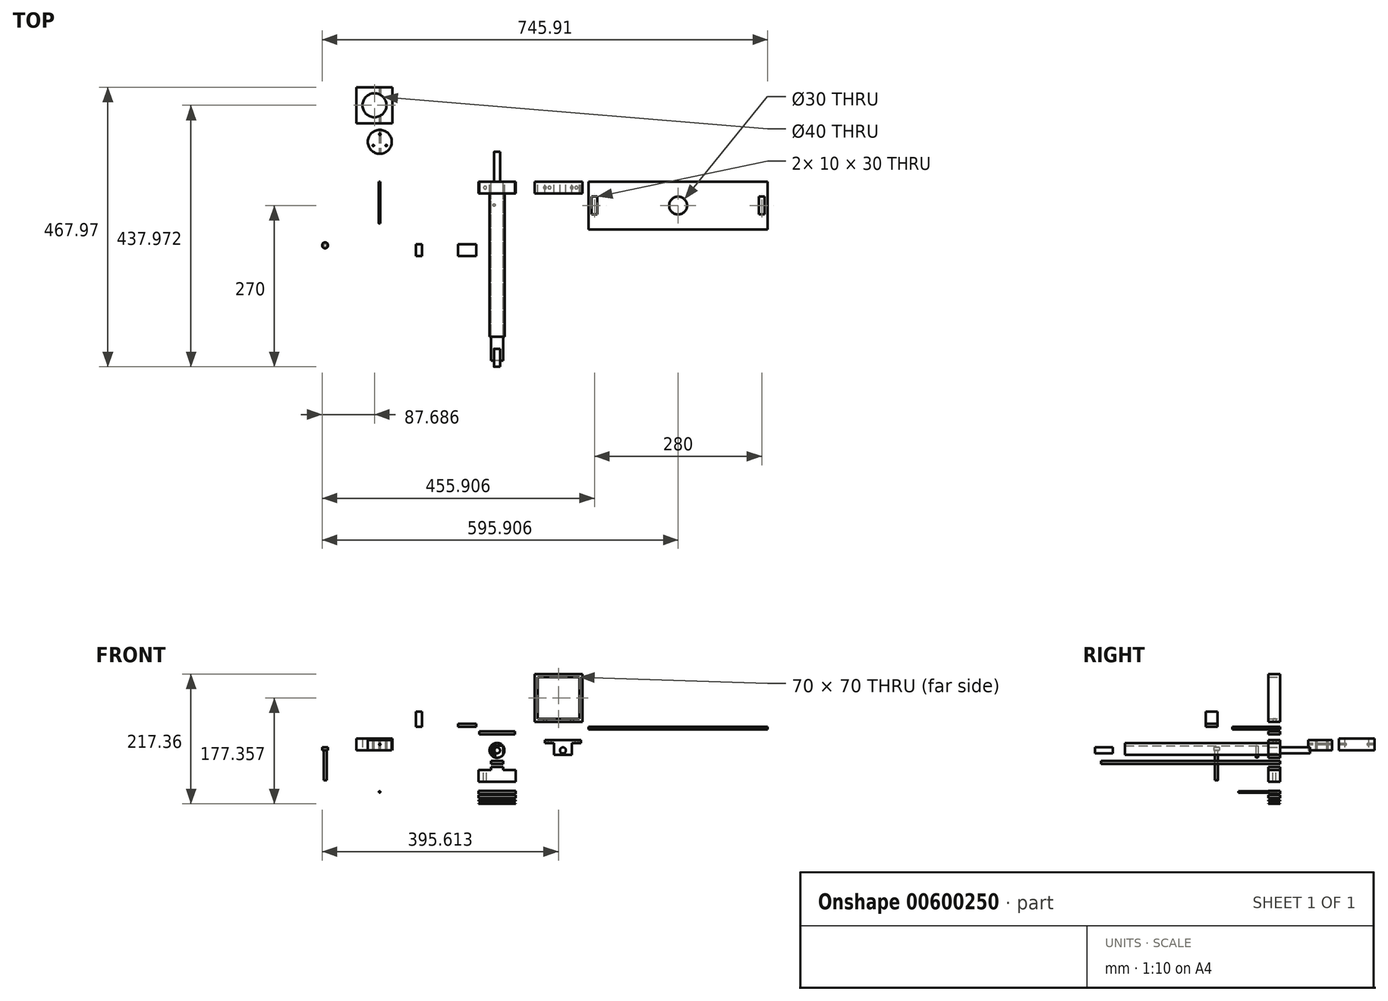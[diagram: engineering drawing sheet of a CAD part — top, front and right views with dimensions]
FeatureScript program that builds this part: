
annotation { "Feature Type Name" : "Feature", "Feature Type Description" : "" }
export const myFeature = defineFeature(function(context is Context, id is Id, definition is map)
    precondition{}
    {
        {
            var Q0;
            Q0=qCreatedBy(makeId("Front.planeOp"),FACE);
            var sketch = newSketch(context, id + "F0", { "sketchPlane" : qUnion([Q0])});
            skCircle(sketch, "E0", {"center": v(0, 0) * mm, "radius": 12.5 * mm});
            skCircle(sketch, "E1", {"center": v(110.3, 0) * mm, "radius": 5 * mm});
            skLineSegment(sketch, "E2.bottom", {"start": v(-30, 31.74) * mm, "end": v(30, 31.74) * mm});
            skLineSegment(sketch, "E2.top", {"start": v(-30, 26.74) * mm, "end": v(30, 26.74) * mm});
            skLineSegment(sketch, "E2.left", {"start": v(-30, 31.74) * mm, "end": v(-30, 26.74) * mm});
            skLineSegment(sketch, "E2.right", {"start": v(30, 31.74) * mm, "end": v(30, 26.74) * mm});
            skPoint(sketch, "E2.middle", {"position": v(0, 29.24) * mm});
            skLineSegment(sketch, "E3", {"start": v(110.3, 10) * mm, "end": v(110.3, -10) * mm, "construction": true});
            skCircle(sketch, "E4", {"center": v(110.3, 0) * mm, "radius": 12.5 * mm, "construction": true});
            skLineSegment(sketch, "E5", {"start": v(97.8, 0) * mm, "end": v(122.8, 0) * mm, "construction": true});
            skLineSegment(sketch, "E6", {"start": v(110.3, 12.5) * mm, "end": v(79.29, 12.5) * mm, "construction": true});
            skLineSegment(sketch, "E7", {"start": v(110.3, 5) * mm, "end": v(79.29, 5) * mm, "construction": true});
            skLineSegment(sketch, "E8", {"start": v(110.3, -5) * mm, "end": v(79.29, -5) * mm, "construction": true});
            skLineSegment(sketch, "E9", {"start": v(110.3, -12.5) * mm, "end": v(79.29, -12.5) * mm, "construction": true});
            skLineSegment(sketch, "E10", {"start": v(110.3, -7.5) * mm, "end": v(125.3, -7.5) * mm});
            skLineSegment(sketch, "E11", {"start": v(110.3, 17.5) * mm, "end": v(140.3, 17.5) * mm});
            skLineSegment(sketch, "E12", {"start": v(125.3, 12.5) * mm, "end": v(140.3, 12.5) * mm});
            skLineSegment(sketch, "E13", {"start": v(125.3, -7.5) * mm, "end": v(125.3, 12.5) * mm});
            skLineSegment(sketch, "E14", {"start": v(140.3, 17.5) * mm, "end": v(140.3, 12.5) * mm});
            skPoint(sketch, "E15.orphan", {"position": v(110.3, 12.5) * mm});
            skLineSegment(sketch, "E16.MirrorCS", {"start": v(95.3, 12.5) * mm, "end": v(80.3, 12.5) * mm});
            skLineSegment(sketch, "E17.MirrorCS", {"start": v(80.3, 17.5) * mm, "end": v(80.3, 12.5) * mm});
            skLineSegment(sketch, "E18.MirrorCS", {"start": v(110.3, 17.5) * mm, "end": v(80.3, 17.5) * mm});
            skLineSegment(sketch, "E19.MirrorCS", {"start": v(95.3, -7.5) * mm, "end": v(95.3, 12.5) * mm});
            skLineSegment(sketch, "E20.MirrorCS", {"start": v(110.3, -7.5) * mm, "end": v(95.3, -7.5) * mm});
            skLineSegment(sketch, "E21.top", {"start": v(0, -27.58) * mm, "end": v(10, -27.58) * mm});
            skLineSegment(sketch, "E22", {"start": v(10.93, -32.58) * mm, "end": v(30.93, -32.58) * mm});
            skLineSegment(sketch, "E23", {"start": v(30.93, -32.58) * mm, "end": v(30.93, -52.58) * mm});
            skLineSegment(sketch, "E24", {"start": v(30.93, -52.58) * mm, "end": v(0, -52.58) * mm});
            skLineSegment(sketch, "E25.MirrorCS", {"start": v(0, -27.58) * mm, "end": v(-10, -27.58) * mm});
            skLineSegment(sketch, "E26.MirrorCS", {"start": v(-10.93, -32.58) * mm, "end": v(-30.93, -32.58) * mm});
            skLineSegment(sketch, "E27.MirrorCS", {"start": v(-30.93, -32.58) * mm, "end": v(-30.93, -52.58) * mm});
            skLineSegment(sketch, "E28.MirrorCS", {"start": v(-30.93, -52.58) * mm, "end": v(0, -52.58) * mm});
            skLineSegment(sketch, "E29", {"start": v(0, -22.52) * mm, "end": v(10, -22.52) * mm});
            skLineSegment(sketch, "E30", {"start": v(10, -22.52) * mm, "end": v(10, -17.52) * mm});
            skLineSegment(sketch, "E31", {"start": v(10, -17.52) * mm, "end": v(0, -17.52) * mm});
            skLineSegment(sketch, "E32.MirrorCS", {"start": v(-10, -17.52) * mm, "end": v(0, -17.52) * mm});
            skLineSegment(sketch, "E33.MirrorCS", {"start": v(0, -22.52) * mm, "end": v(-10, -22.52) * mm});
            skLineSegment(sketch, "E34.MirrorCS", {"start": v(-10, -22.52) * mm, "end": v(-10, -17.52) * mm});
            skLineSegment(sketch, "E35.bottom", {"start": v(137.73, 52.7) * mm, "end": v(67.73, 52.7) * mm});
            skLineSegment(sketch, "E35.top", {"start": v(137.73, 122.7) * mm, "end": v(67.73, 122.7) * mm});
            skLineSegment(sketch, "E35.left", {"start": v(137.73, 52.7) * mm, "end": v(137.73, 122.7) * mm});
            skLineSegment(sketch, "E35.right", {"start": v(67.73, 52.7) * mm, "end": v(67.73, 122.7) * mm});
            skPoint(sketch, "E35.middle", {"position": v(102.73, 87.7) * mm});
            skLineSegment(sketch, "E36.bottom", {"start": v(62.73, 127.7) * mm, "end": v(142.73, 127.7) * mm});
            skLineSegment(sketch, "E36.top", {"start": v(62.73, 47.7) * mm, "end": v(142.73, 47.7) * mm});
            skLineSegment(sketch, "E36.left", {"start": v(62.73, 127.7) * mm, "end": v(62.73, 47.7) * mm});
            skLineSegment(sketch, "E36.right", {"start": v(142.73, 127.7) * mm, "end": v(142.73, 47.7) * mm});
            skLineSegment(sketch, "E37.bottom", {"start": v(-30.93, -79.86) * mm, "end": v(30.93, -79.86) * mm});
            skLineSegment(sketch, "E37.top", {"start": v(-30.93, -74.86) * mm, "end": v(30.93, -74.86) * mm});
            skLineSegment(sketch, "E37.left", {"start": v(-30.93, -79.86) * mm, "end": v(-30.93, -74.86) * mm});
            skLineSegment(sketch, "E37.right", {"start": v(30.93, -79.86) * mm, "end": v(30.93, -74.86) * mm});
            skLineSegment(sketch, "E38.MirrorCS", {"start": v(-30.74, -88.65) * mm, "end": v(31.12, -88.65) * mm});
            skLineSegment(sketch, "E39.MirrorCS", {"start": v(-30.74, -89.65) * mm, "end": v(31.12, -89.65) * mm});
            skLineSegment(sketch, "E40", {"start": v(-30.93, -82.76) * mm, "end": v(30.93, -82.76) * mm});
            skLineSegment(sketch, "E41", {"start": v(30.93, -82.76) * mm, "end": v(30.93, -84.76) * mm});
            skLineSegment(sketch, "E42", {"start": v(30.93, -84.76) * mm, "end": v(-30.93, -84.76) * mm});
            skLineSegment(sketch, "E43", {"start": v(-30.93, -84.76) * mm, "end": v(-30.93, -82.76) * mm});
            skLineSegment(sketch, "E44", {"start": v(-30.74, -88.65) * mm, "end": v(-30.74, -89.65) * mm});
            skLineSegment(sketch, "E45", {"start": v(31.12, -88.65) * mm, "end": v(31.12, -89.65) * mm});
            skLineSegment(sketch, "E46", {"start": v(-30.93, -72.74) * mm, "end": v(30.93, -72.74) * mm});
            skLineSegment(sketch, "E47", {"start": v(30.93, -72.74) * mm, "end": v(30.93, -67.74) * mm});
            skLineSegment(sketch, "E48", {"start": v(30.93, -67.74) * mm, "end": v(-30.93, -67.74) * mm});
            skLineSegment(sketch, "E49", {"start": v(-30.93, -67.74) * mm, "end": v(-30.93, -72.74) * mm});
            skLineSegment(sketch, "E50", {"start": v(-10, -27.58) * mm, "end": v(-10, -32.58) * mm});
            skLineSegment(sketch, "E51", {"start": v(-10, -32.58) * mm, "end": v(-10.93, -32.58) * mm});
            skPoint(sketch, "E52.MirrorCS.end.orphan", {"position": v(-10, -27.58) * mm});
            skPoint(sketch, "E52.MirrorCS.start.orphan", {"position": v(-10.93, -32.58) * mm});
            skLineSegment(sketch, "E53", {"start": v(10, -27.58) * mm, "end": v(10, -32.58) * mm});
            skLineSegment(sketch, "E54", {"start": v(10, -32.58) * mm, "end": v(10.93, -32.58) * mm});
            skLineSegment(sketch, "E55.left", {"start": v(194.47, 95.4) * mm, "end": v(194.47, 97.9) * mm});
            skLineSegment(sketch, "E56.bottom", {"start": v(-122.7, 157) * mm, "end": v(-422.7, 157) * mm});
            skLineSegment(sketch, "E56.top", {"start": v(-122.7, 159.5) * mm, "end": v(-422.7, 159.5) * mm});
            skLineSegment(sketch, "E56.left", {"start": v(-122.7, 157) * mm, "end": v(-122.7, 159.5) * mm});
            skLineSegment(sketch, "E56.right", {"start": v(-422.7, 157) * mm, "end": v(-422.7, 159.5) * mm});
            skLineSegment(sketch, "E57", {"start": v(-272.7, 150) * mm, "end": v(-272.7, 153.49) * mm, "construction": true});
            skPoint(sketch, "E57.startSnap0", {"position": v(-272.7, 157) * mm});
            skSolve(sketch);
        }
        {
            var Q0;
            Q0=makeQuery(id+"F0.imprint","IMPRINT",FACE,{"disambiguationData":[TD([[makeQuery(id+"F0.imprint","IMPRINT",EDGE,{"derivedFrom":sQuery(id+"F0.wireOp",EDGE,"E1")}),-1.0]])]});
            var Q1;
            Q1=makeQuery(id+"F0.imprint","IMPRINT",FACE,{"disambiguationData":[TD([[makeQuery(id+"F0.imprint","IMPRINT",EDGE,{"derivedFrom":sQuery(id+"F0.wireOp",EDGE,"E2.bottom")}),-1.0]])]});
            var Q2;
            Q2=makeQuery(id+"F0.imprint","IMPRINT",FACE,{"disambiguationData":[TD([[makeQuery(id+"F0.imprint","IMPRINT",EDGE,{"derivedFrom":sQuery(id+"F0.wireOp",EDGE,"E21.top")}),-1.0]])]});
            var Q3;
            Q3=makeQuery(id+"F0.imprint","IMPRINT",FACE,{"disambiguationData":[TD([[makeQuery(id+"F0.imprint","IMPRINT",EDGE,{"derivedFrom":sQuery(id+"F0.wireOp",EDGE,"E35.bottom")}),1.0]])]});
            var Q4;
            Q4=makeQuery(id+"F0.imprint","IMPRINT",FACE,{"disambiguationData":[TD([[makeQuery(id+"F0.imprint","IMPRINT",EDGE,{"derivedFrom":sQuery(id+"F0.wireOp",EDGE,"E37.bottom")}),1.0]])]});
            var Q5;
            Q5=makeQuery(id+"F0.imprint","IMPRINT",FACE,{"disambiguationData":[TD([[makeQuery(id+"F0.imprint","IMPRINT",EDGE,{"derivedFrom":sQuery(id+"F0.wireOp",EDGE,"E38.MirrorCS")}),-1.0]])]});
            var Q6;
            Q6=makeQuery(id+"F0.imprint","IMPRINT",FACE,{"disambiguationData":[TD([[makeQuery(id+"F0.imprint","IMPRINT",EDGE,{"derivedFrom":sQuery(id+"F0.wireOp",EDGE,"E40")}),-1.0]])]});
            var Q7;
            Q7=makeQuery(id+"F0.imprint","IMPRINT",FACE,{"disambiguationData":[TD([[makeQuery(id+"F0.imprint","IMPRINT",EDGE,{"derivedFrom":sQuery(id+"F0.wireOp",EDGE,"E46")}),1.0]])]});
            var Q8;
            {var subQ5=sQuery(id+"F0.wireOp",EDGE,"E55.right");Q8=makeQuery(id+"F0.imprint","IMPRINT",FACE,{"disambiguationData":[TD([[makeQuery(id+"F0.imprint","IMPRINT",EDGE,{"derivedFrom":subQ5}),-1.0]])]});}
            extrude(context, id + "F1", {"entities" : qUnion([Q0, Q1, Q2, Q3, Q4, Q5, Q6, Q7, Q8]), "depth" : 20 * mm, "offsetDistance" : 25 * mm});
        }
        {
            var Q0;
            Q0=makeQuery(id+"F0.imprint","IMPRINT",FACE,{"disambiguationData":[TD([[makeQuery(id+"F0.imprint","IMPRINT",EDGE,{"derivedFrom":sQuery(id+"F0.wireOp",EDGE,"E0")}),1.0]])]});
            extrude(context, id + "F2", {"entities" : qUnion([Q0]), "depth" : 260 * mm, "offsetDistance" : 25 * mm});
        }
        {
            var Q0;
            Q0=makeQuery(id+"F2.opExtrude","CAP_FACE",FACE,{"disambiguationData":[OSD([sQuery(id+"F0.wireOp",EDGE,"E0")])],"isStart":false});
            var sketch = newSketch(context, id + "F3", { "sketchPlane" : qUnion([Q0])});
            skCircle(sketch, "E58", {"center": v(0, 0) * mm, "radius": 5 * mm});
            skSolve(sketch);
        }
        {
            var Q0;
            Q0=makeQuery(id+"F3.imprint","IMPRINT",FACE,{"disambiguationData":[TD([[makeQuery(id+"F3.imprint","IMPRINT",EDGE,{"derivedFrom":sQuery(id+"F3.wireOp",EDGE,"E58")}),1.0]])]});
            extrude(context, id + "F4", {"entities" : qUnion([Q0]), "operationType" : NewBodyOperationType.ADD, "depth" : 50 * mm, "offsetDistance" : 25 * mm});
        }
        {
            var Q0;
            Q0=makeQuery(id+"F0.imprint","IMPRINT",FACE,{"disambiguationData":[TD([[makeQuery(id+"F0.imprint","IMPRINT",EDGE,{"derivedFrom":sQuery(id+"F0.wireOp",EDGE,"E29")}),1.0]])]});
            extrude(context, id + "F5", {"entities" : qUnion([Q0]), "depth" : 300 * mm, "offsetDistance" : 25 * mm});
        }
        {
            var Q0;
            Q0=makeQuery(id+"F1.opExtrude","SWEPT_FACE",FACE,{"disambiguationData":[OSD([sQuery(id+"F0.wireOp",EDGE,"E26.MirrorCS")])]});
            var sketch = newSketch(context, id + "F6", { "sketchPlane" : qUnion([Q0])});
            skCircle(sketch, "E59", {"center": v(-20, -10) * mm, "radius": 2.5 * mm});
            skSolve(sketch);
        }
        {
            var Q0;
            Q0=makeQuery(id+"F6.imprint","IMPRINT",FACE,{"disambiguationData":[TD([[makeQuery(id+"F6.imprint","IMPRINT",EDGE,{"derivedFrom":sQuery(id+"F6.wireOp",EDGE,"E59")}),1.0]])]});
            var Q1;
            Q1=makeQuery(id+"FNYWGUJzlf6PVvf_4.imprint","IMPRINT",FACE,{"disambiguationData":[TD([[makeQuery(id+"FNYWGUJzlf6PVvf_4.imprint","IMPRINT",EDGE,{"derivedFrom":sQuery(id+"FNYWGUJzlf6PVvf_4.wireOp",EDGE,"JrdPBHnR-5tIZ-cZ5f-IPz8-CMVoVNEgzM20")}),1.0]])]});
            extrude(context, id + "F7", {"entities" : qUnion([Q0, Q1]), "operationType" : NewBodyOperationType.REMOVE, "oppositeDirection" : true, "depth" : 25 * mm, "offsetDistance" : 25 * mm});
        }
        {
            var Q0;
            Q0=makeQuery(id+"F1.opExtrude","SWEPT_FACE",FACE,{"disambiguationData":[OSD([sQuery(id+"F0.wireOp",EDGE,"E12")])]});
            var sketch = newSketch(context, id + "F8", { "sketchPlane" : qUnion([Q0])});
            skCircle(sketch, "E60", {"center": v(132.8, 10) * mm, "radius": 2.5 * mm});
            skPoint(sketch, "E60.centerSnap0", {"position": v(132.8, 20) * mm});
            skPoint(sketch, "E60.centerSnap1", {"position": v(125.3, 10) * mm});
            skSolve(sketch);
        }
        {
            var Q0;
            Q0=makeQuery(id+"F1.opExtrude","SWEPT_FACE",FACE,{"disambiguationData":[OSD([sQuery(id+"F0.wireOp",EDGE,"E16.MirrorCS")])]});
            var sketch = newSketch(context, id + "F9", { "sketchPlane" : qUnion([Q0])});
            skCircle(sketch, "E61", {"center": v(87.8, 10) * mm, "radius": 2.5 * mm});
            skPoint(sketch, "E61.centerSnap0", {"position": v(80.3, 10) * mm});
            skPoint(sketch, "E61.centerSnap1", {"position": v(87.8, 20) * mm});
            skSolve(sketch);
        }
        {
            var Q0;
            Q0=makeQuery(id+"F9.imprint","IMPRINT",FACE,{"disambiguationData":[TD([[makeQuery(id+"F9.imprint","IMPRINT",EDGE,{"derivedFrom":sQuery(id+"F9.wireOp",EDGE,"E61")}),1.0]])]});
            var Q1;
            Q1=makeQuery(id+"F8.imprint","IMPRINT",FACE,{"disambiguationData":[TD([[makeQuery(id+"F8.imprint","IMPRINT",EDGE,{"derivedFrom":sQuery(id+"F8.wireOp",EDGE,"E60")}),1.0]])]});
            extrude(context, id + "F10", {"entities" : qUnion([Q0, Q1]), "operationType" : NewBodyOperationType.REMOVE, "oppositeDirection" : true, "depth" : 25 * mm, "offsetDistance" : 25 * mm});
        }
        {
            var Q0;
            Q0=makeQuery(id+"F5.opExtrude","SWEPT_FACE",FACE,{"disambiguationData":[OSD([sQuery(id+"F0.wireOp",EDGE,"E31"),sQuery(id+"F0.wireOp",EDGE,"E32.MirrorCS")])]});
            var sketch = newSketch(context, id + "F11", { "sketchPlane" : qUnion([Q0])});
            skLineSegment(sketch, "E62", {"start": v(-10, -280) * mm, "end": v(10, -280) * mm});
            skCircle(sketch, "E63", {"center": v(5, -39.13) * mm, "radius": 1.93 * mm});
            skPoint(sketch, "E64.orphan", {"position": v(0, -300) * mm});
            skCircle(sketch, "E65.MirrorC", {"center": v(-5, -39.13) * mm, "radius": 1.93 * mm});
            skLineSegment(sketch, "E66", {"start": v(10, -20) * mm, "end": v(-10, -20) * mm});
            skSolve(sketch);
        }
        {
            var Q0;
            Q0=makeQuery(id+"F11.imprint","IMPRINT",FACE,{"disambiguationData":[TD([[makeQuery(id+"F11.imprint","IMPRINT",EDGE,{"derivedFrom":sQuery(id+"F11.wireOp",EDGE,"E65.MirrorC")}),-1.0]])]});
            var Q1;
            Q1=makeQuery(id+"F11.imprint","IMPRINT",FACE,{"disambiguationData":[TD([[makeQuery(id+"F11.imprint","IMPRINT",EDGE,{"derivedFrom":sQuery(id+"F11.wireOp",EDGE,"E63")}),1.0]])]});
            extrude(context, id + "F12", {"entities" : qUnion([Q0, Q1]), "operationType" : NewBodyOperationType.REMOVE, "depth" : 25 * mm, "offsetDistance" : 25 * mm});
        }
        {
            var Q0;
            Q0=makeQuery(id+"F1.opExtrude","SWEPT_FACE",FACE,{"disambiguationData":[OSD([sQuery(id+"F0.wireOp",EDGE,"E36.top")])]});
            var sketch = newSketch(context, id + "F13", { "sketchPlane" : qUnion([Q0])});
            skCircle(sketch, "E67", {"center": v(80.23, 10) * mm, "radius": 2.5 * mm});
            skCircle(sketch, "E68", {"center": v(125.23, 10) * mm, "radius": 2.5 * mm});
            skLineSegment(sketch, "E69", {"start": v(62.73, 20) * mm, "end": v(142.73, 20) * mm, "construction": true});
            skLineSegment(sketch, "E70", {"start": v(142.73, 20) * mm, "end": v(142.73, 0) * mm, "construction": true});
            skLineSegment(sketch, "E71", {"start": v(142.73, 0) * mm, "end": v(62.73, 0) * mm, "construction": true});
            skLineSegment(sketch, "E72", {"start": v(62.73, 0) * mm, "end": v(62.73, 20) * mm, "construction": true});
            skLineSegment(sketch, "E73", {"start": v(67.73, 20) * mm, "end": v(67.73, 0) * mm, "construction": true});
            skLineSegment(sketch, "E74", {"start": v(137.73, 20) * mm, "end": v(137.73, 0) * mm, "construction": true});
            skSolve(sketch);
        }
        {
            var Q0;
            Q0=makeQuery(id+"F2.opExtrude","CAP_FACE",FACE,{"disambiguationData":[OSD([sQuery(id+"F0.wireOp",EDGE,"E0")])],"isStart":true});
            var sketch = newSketch(context, id + "F14", { "sketchPlane" : qUnion([Q0])});
            skCircle(sketch, "E75", {"center": v(0, 0) * mm, "radius": 5 * mm});
            skSolve(sketch);
        }
        {
            var Q0;
            Q0=qSketchRegion(id+"F14",true);
            extrude(context, id + "F15", {"entities" : qUnion([Q0]), "operationType" : NewBodyOperationType.ADD, "depth" : 50 * mm, "offsetDistance" : 25 * mm});
        }
        {
            var Q0;
            Q0=qCreatedBy(makeId("Front.planeOp"),FACE);
            var sketch = newSketch(context, id + "F16", { "sketchPlane" : qUnion([Q0])});
            skLineSegment(sketch, "E76.bottom", {"start": v(153.03, 39.78) * mm, "end": v(453.03, 39.78) * mm});
            skLineSegment(sketch, "E76.top", {"start": v(153.03, 34.78) * mm, "end": v(453.03, 34.78) * mm});
            skLineSegment(sketch, "E76.left", {"start": v(153.03, 39.78) * mm, "end": v(153.03, 34.78) * mm});
            skLineSegment(sketch, "E76.right", {"start": v(453.03, 39.78) * mm, "end": v(453.03, 34.78) * mm});
            skSolve(sketch);
        }
        {
            var Q0;
            Q0=makeQuery(id+"F16.imprint","IMPRINT",FACE,{"disambiguationData":[TD([[makeQuery(id+"F16.imprint","IMPRINT",EDGE,{"derivedFrom":sQuery(id+"F16.wireOp",EDGE,"E76.bottom")}),-1.0]])]});
            extrude(context, id + "F17", {"entities" : qUnion([Q0]), "depth" : 80 * mm, "offsetDistance" : 25 * mm});
        }
        {
            var Q0;
            Q0=makeQuery(id+"F17.opExtrude","SWEPT_FACE",FACE,{"disambiguationData":[OSD([sQuery(id+"F16.wireOp",EDGE,"E76.bottom")])]});
            var sketch = newSketch(context, id + "F18", { "sketchPlane" : qUnion([Q0])});
            skLineSegment(sketch, "E77", {"start": v(173.03, 0) * mm, "end": v(173.03, -80) * mm});
            skLineSegment(sketch, "E78.bottom", {"start": v(158.03, -25) * mm, "end": v(168.03, -25) * mm});
            skLineSegment(sketch, "E78.top", {"start": v(158.03, -55) * mm, "end": v(168.03, -55) * mm});
            skLineSegment(sketch, "E78.left", {"start": v(158.03, -25) * mm, "end": v(158.03, -55) * mm});
            skLineSegment(sketch, "E78.right", {"start": v(168.03, -25) * mm, "end": v(168.03, -55) * mm});
            skPoint(sketch, "E78.middle", {"position": v(163.03, -40) * mm});
            skLineSegment(sketch, "E79", {"start": v(303.03, 0) * mm, "end": v(303.03, -80) * mm, "construction": true});
            skLineSegment(sketch, "E80.MirrorCS", {"start": v(438.03, -25) * mm, "end": v(438.03, -55) * mm});
            skLineSegment(sketch, "E81.MirrorCS", {"start": v(448.03, -25) * mm, "end": v(438.03, -25) * mm});
            skLineSegment(sketch, "E82.MirrorCS", {"start": v(448.03, -25) * mm, "end": v(448.03, -55) * mm});
            skLineSegment(sketch, "E83.MirrorCS", {"start": v(448.03, -55) * mm, "end": v(438.03, -55) * mm});
            skLineSegment(sketch, "E84.MirrorCS", {"start": v(433.03, 0) * mm, "end": v(433.03, -80) * mm});
            skLineSegment(sketch, "E85.bottom", {"start": v(-65.07, -104.85) * mm, "end": v(-35.07, -104.85) * mm});
            skLineSegment(sketch, "E85.top", {"start": v(-65.07, -124.85) * mm, "end": v(-35.07, -124.85) * mm});
            skLineSegment(sketch, "E85.left", {"start": v(-65.07, -104.85) * mm, "end": v(-65.07, -124.85) * mm});
            skLineSegment(sketch, "E85.right", {"start": v(-35.07, -104.85) * mm, "end": v(-35.07, -124.85) * mm});
            skLineSegment(sketch, "E86.bottom", {"start": v(-135.53, -104.85) * mm, "end": v(-125.53, -104.85) * mm});
            skLineSegment(sketch, "E86.top", {"start": v(-135.53, -124.85) * mm, "end": v(-125.53, -124.85) * mm});
            skLineSegment(sketch, "E86.left", {"start": v(-135.53, -104.85) * mm, "end": v(-135.53, -124.85) * mm});
            skLineSegment(sketch, "E86.right", {"start": v(-125.53, -104.85) * mm, "end": v(-125.53, -124.85) * mm});
            skCircle(sketch, "E87", {"center": v(303.03, -40) * mm, "radius": 15 * mm});
            skSolve(sketch);
        }
        {
            var Q0;
            Q0=qCreatedBy(makeId("Top.planeOp"),FACE);
            var sketch = newSketch(context, id + "F19", { "sketchPlane" : qUnion([Q0])});
            skCircle(sketch, "E88", {"center": v(-196.27, 66.8) * mm, "radius": 20 * mm});
            skLineSegment(sketch, "E89.bottom", {"start": v(-235.2, 97.97) * mm, "end": v(-175.2, 97.97) * mm});
            skLineSegment(sketch, "E89.top", {"start": v(-235.2, 157.97) * mm, "end": v(-175.2, 157.97) * mm});
            skLineSegment(sketch, "E89.left", {"start": v(-235.2, 97.97) * mm, "end": v(-235.2, 157.97) * mm});
            skLineSegment(sketch, "E89.right", {"start": v(-175.2, 97.97) * mm, "end": v(-175.2, 157.97) * mm});
            skCircle(sketch, "E90", {"center": v(-205.2, 127.97) * mm, "radius": 20 * mm});
            skPoint(sketch, "E90.centerSnap0", {"position": v(-175.2, 127.97) * mm});
            skPoint(sketch, "E90.centerSnap1", {"position": v(-205.2, 97.97) * mm});
            skLineSegment(sketch, "E91", {"start": v(-196.27, 46.8) * mm, "end": v(-222.09, 46.8) * mm});
            skSolve(sketch);
        }
        {
            var Q0;
            Q0=makeQuery(id+"F19.imprint","IMPRINT",FACE,{"disambiguationData":[TD([[makeQuery(id+"F19.imprint","IMPRINT",EDGE,{"derivedFrom":sQuery(id+"F19.wireOp",EDGE,"E88")}),1.0]])]});
            extrude(context, id + "F20", {"entities" : qUnion([Q0]), "depth" : 17.5 * mm, "offsetDistance" : 25 * mm});
        }
        {
            var Q0;
            Q0=makeQuery(id+"F19.imprint","IMPRINT",FACE,{"disambiguationData":[TD([[makeQuery(id+"F19.imprint","IMPRINT",EDGE,{"derivedFrom":sQuery(id+"F19.wireOp",EDGE,"E89.bottom")}),1.0]])]});
            extrude(context, id + "F21", {"entities" : qUnion([Q0]), "depth" : 20 * mm, "offsetDistance" : 25 * mm});
        }
        {
            var Q0;
            Q0=makeQuery(id+"F18.imprint","IMPRINT",FACE,{"disambiguationData":[TD([[makeQuery(id+"F18.imprint","IMPRINT",EDGE,{"derivedFrom":sQuery(id+"F18.wireOp",EDGE,"E78.bottom")}),-1.0]])]});
            var Q1;
            Q1=makeQuery(id+"F18.imprint","IMPRINT",FACE,{"disambiguationData":[TD([[makeQuery(id+"F18.imprint","IMPRINT",EDGE,{"derivedFrom":sQuery(id+"F18.wireOp",EDGE,"E80.MirrorCS")}),1.0]])]});
            var Q2;
            Q2=makeQuery(id+"F18.imprint","IMPRINT",FACE,{"disambiguationData":[TD([[makeQuery(id+"F18.imprint","IMPRINT",EDGE,{"derivedFrom":sQuery(id+"F18.wireOp",EDGE,"E87")}),1.0]])]});
            extrude(context, id + "F22", {"entities" : qUnion([Q0, Q1, Q2]), "operationType" : NewBodyOperationType.REMOVE, "endBound" : BoundingType.THROUGH_ALL, "oppositeDirection" : true, "depth" : 25 * mm, "offsetDistance" : 25 * mm});
        }
        {
            var Q0;
            Q0=makeQuery(id+"F18.imprint","IMPRINT",FACE,{"disambiguationData":[TD([[makeQuery(id+"F18.imprint","IMPRINT",EDGE,{"derivedFrom":sQuery(id+"F18.wireOp",EDGE,"E86.bottom")}),-1.0]])]});
            extrude(context, id + "F23", {"entities" : qUnion([Q0]), "depth" : 25 * mm, "offsetDistance" : 25 * mm});
        }
        {
            var Q0;
            Q0=makeQuery(id+"F18.imprint","IMPRINT",FACE,{"disambiguationData":[TD([[makeQuery(id+"F18.imprint","IMPRINT",EDGE,{"derivedFrom":sQuery(id+"F18.wireOp",EDGE,"E85.bottom")}),-1.0]])]});
            extrude(context, id + "F24", {"entities" : qUnion([Q0]), "depth" : 5 * mm, "offsetDistance" : 25 * mm});
        }
        {
            var Q0;
            Q0=makeQuery(id+"F13.imprint","IMPRINT",FACE,{"disambiguationData":[TD([[makeQuery(id+"F13.imprint","IMPRINT",EDGE,{"derivedFrom":sQuery(id+"F13.wireOp",EDGE,"E68")}),1.0]])]});
            var Q1;
            Q1=makeQuery(id+"F13.imprint","IMPRINT",FACE,{"disambiguationData":[TD([[makeQuery(id+"F13.imprint","IMPRINT",EDGE,{"derivedFrom":sQuery(id+"F13.wireOp",EDGE,"E67")}),1.0]])]});
            extrude(context, id + "F25", {"entities" : qUnion([Q0, Q1]), "operationType" : NewBodyOperationType.REMOVE, "endBound" : BoundingType.UP_TO_NEXT, "oppositeDirection" : true, "depth" : 25 * mm, "offsetDistance" : 25 * mm});
        }
        {
            var Q0;
            Q0=qCreatedBy(makeId("Top.planeOp"),FACE);
            var sketch = newSketch(context, id + "F26", { "sketchPlane" : qUnion([Q0])});
            skCircle(sketch, "E92", {"center": v(-287.88, -106.71) * mm, "radius": 5 * mm});
            skSolve(sketch);
        }
        {
            var Q0;
            Q0=makeQuery(id+"F26.imprint","IMPRINT",FACE,{"disambiguationData":[TD([[makeQuery(id+"F26.imprint","IMPRINT",EDGE,{"derivedFrom":sQuery(id+"F26.wireOp",EDGE,"E92")}),1.0]])]});
            extrude(context, id + "F27", {"entities" : qUnion([Q0]), "depth" : 5 * mm, "offsetDistance" : 25 * mm});
        }
        {
            var Q0;
            Q0=makeQuery(id+"F26.imprint","IMPRINT",FACE,{"disambiguationData":[TD([[makeQuery(id+"F26.imprint","IMPRINT",EDGE,{"derivedFrom":sQuery(id+"F26.wireOp",EDGE,"E92")}),1.0]])]});
            var sketch = newSketch(context, id + "F28", { "sketchPlane" : qUnion([Q0])});
            skCircle(sketch, "E93", {"center": v(-287.73, -106.85) * mm, "radius": 2.5 * mm});
            skSolve(sketch);
        }
        {
            var Q0;
            Q0=makeQuery(id+"F28.imprint","IMPRINT",FACE,{"disambiguationData":[TD([[makeQuery(id+"F28.imprint","IMPRINT",EDGE,{"derivedFrom":sQuery(id+"F28.wireOp",EDGE,"E93")}),1.0]])]});
            extrude(context, id + "F29", {"entities" : qUnion([Q0]), "operationType" : NewBodyOperationType.ADD, "oppositeDirection" : true, "depth" : 50 * mm, "offsetDistance" : 25 * mm});
        }
        {
            var Q0;
            Q0=sQuery(id+"F19.wireOp",EDGE,"E91");
            extrude(context, id + "F30", {"bodyType" : ToolBodyType.SURFACE, "surfaceEntities" : qUnion([Q0]), "depth" : 20 * mm, "offsetDistance" : 25 * mm});
        }
        {
            var Q0;
            Q0=makeQuery(id+"F30.opExtrude","SWEPT_FACE",FACE,{"disambiguationData":[OSD([sQuery(id+"F19.wireOp",EDGE,"E91")])]});
            var sketch = newSketch(context, id + "F31", { "sketchPlane" : qUnion([Q0])});
            skCircle(sketch, "E94", {"center": v(196.27, 10) * mm, "radius": 1.25 * mm});
            skSolve(sketch);
        }
        {
            var Q0;
            {var subQ0=sQuery(id+"F31.wireOp",EDGE,"E94");var subQ1=makeQuery(id+"F30.opExtrude","SWEPT_EDGE",EDGE,{"disambiguationData":[OSD([sQuery(id+"F19.wireOp",VERTEX,"E91.start")])]});var subQ2=makeQuery(id+"F31.imprint","INTERSECT",VERTEX,{"disambiguationData":[OD(0.0)],"derivedFrom":[subQ1,subQ0]});Q0=makeQuery(id+"F31.imprint","IMPRINT",FACE,{"disambiguationData":[TD([[makeQuery(id+"F31.imprint","IMPRINT",EDGE,{"disambiguationData":[TD([[subQ2,-1.0]])],"derivedFrom":subQ0}),1.0]])]});}
            var Q1;
            {var subQ0=sQuery(id+"F31.wireOp",EDGE,"E94");var subQ1=makeQuery(id+"F30.opExtrude","SWEPT_EDGE",EDGE,{"disambiguationData":[OSD([sQuery(id+"F19.wireOp",VERTEX,"E91.start")])]});var subQ2=makeQuery(id+"F31.imprint","INTERSECT",VERTEX,{"disambiguationData":[OD(0.0)],"derivedFrom":[subQ1,subQ0]});Q1=makeQuery(id+"F31.imprint","IMPRINT",FACE,{"disambiguationData":[TD([[makeQuery(id+"F31.imprint","IMPRINT",EDGE,{"disambiguationData":[TD([[subQ2,1.0]])],"derivedFrom":subQ0}),1.0]])]});}
            extrude(context, id + "F32", {"entities" : qUnion([Q0, Q1]), "operationType" : NewBodyOperationType.REMOVE, "endBound" : BoundingType.THROUGH_ALL, "depth" : 25 * mm, "offsetDistance" : 25 * mm});
        }
        {
            var Q0;
            Q0=qCreatedBy(makeId("Front.planeOp"),FACE);
            var sketch = newSketch(context, id + "F33", { "sketchPlane" : qUnion([Q0])});
            skCircle(sketch, "E95", {"center": v(-196.47, -69.5) * mm, "radius": 1.25 * mm});
            skSolve(sketch);
        }
        {
            var Q0;
            Q0=makeQuery(id+"F33.imprint","IMPRINT",FACE,{"disambiguationData":[TD([[makeQuery(id+"F33.imprint","IMPRINT",EDGE,{"derivedFrom":sQuery(id+"F33.wireOp",EDGE,"E95")}),1.0]])]});
            extrude(context, id + "F34", {"entities" : qUnion([Q0]), "depth" : 70 * mm, "offsetDistance" : 25 * mm});
        }
        {
            var Q0;
            Q0=makeQuery(id+"F20.opExtrude","CAP_FACE",FACE,{"disambiguationData":[OSD([sQuery(id+"F19.wireOp",EDGE,"E88")])],"isStart":false});
            var sketch = newSketch(context, id + "F35", { "sketchPlane" : qUnion([Q0])});
            skCircle(sketch, "E96", {"center": v(-196.27, 79.3) * mm, "radius": 1.25 * mm});
            skCircle(sketch, "E97", {"center": v(-185.44, 60.55) * mm, "radius": 1.25 * mm});
            skCircle(sketch, "E98", {"center": v(-207.1, 60.55) * mm, "radius": 1.25 * mm});
            skCircle(sketch, "E99", {"center": v(-196.27, 66.8) * mm, "radius": 12.5 * mm, "construction": true});
            skSolve(sketch);
        }
        {
            var Q0;
            Q0=makeQuery(id+"F35.imprint","IMPRINT",FACE,{"disambiguationData":[TD([[makeQuery(id+"F35.imprint","IMPRINT",EDGE,{"derivedFrom":sQuery(id+"F35.wireOp",EDGE,"E96")}),1.0]])]});
            var Q1;
            Q1=makeQuery(id+"F35.imprint","IMPRINT",FACE,{"disambiguationData":[TD([[makeQuery(id+"F35.imprint","IMPRINT",EDGE,{"derivedFrom":sQuery(id+"F35.wireOp",EDGE,"E97")}),1.0]])]});
            var Q2;
            Q2=makeQuery(id+"F35.imprint","IMPRINT",FACE,{"disambiguationData":[TD([[makeQuery(id+"F35.imprint","IMPRINT",EDGE,{"derivedFrom":sQuery(id+"F35.wireOp",EDGE,"E98")}),1.0]])]});
            extrude(context, id + "F36", {"entities" : qUnion([Q0, Q1, Q2]), "operationType" : NewBodyOperationType.REMOVE, "endBound" : BoundingType.THROUGH_ALL, "oppositeDirection" : true, "depth" : 25 * mm, "offsetDistance" : 25 * mm});
        }
    });
